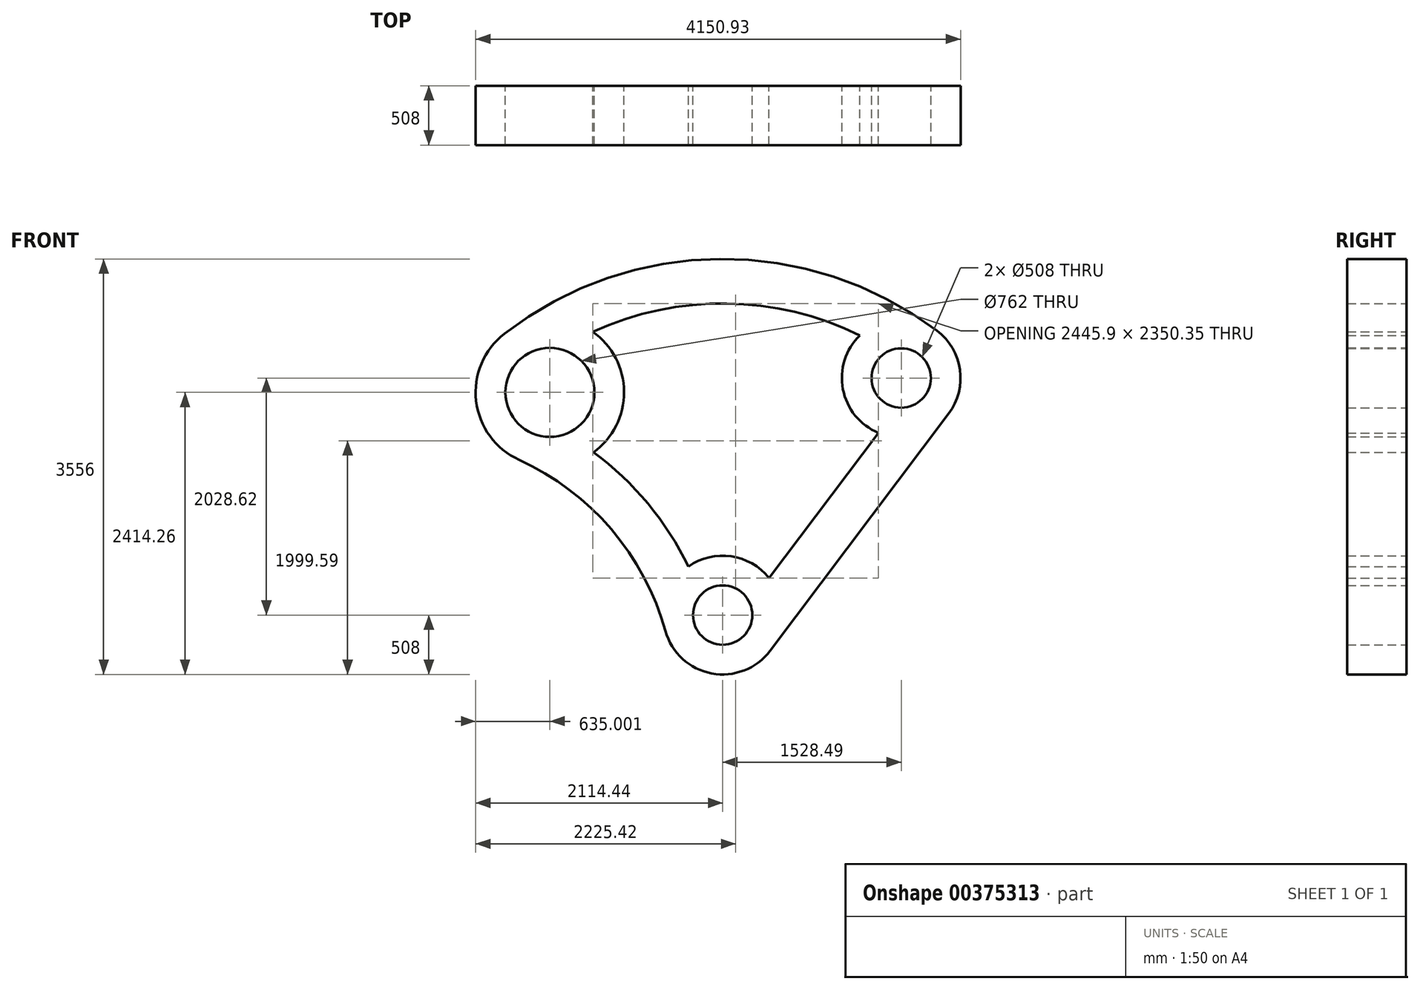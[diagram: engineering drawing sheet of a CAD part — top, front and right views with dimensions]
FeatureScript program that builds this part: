
annotation { "Feature Type Name" : "Feature", "Feature Type Description" : "" }
export const myFeature = defineFeature(function(context is Context, id is Id, definition is map)
    precondition{}
    {
        {
            var Q0;
            Q0=qCreatedBy(makeId("Front.planeOp"),FACE);
            var sketch = newSketch(context, id + "F0", { "sketchPlane" : qUnion([Q0])});
            skCircle(sketch, "E0", {"center": v(0, 0) * mm, "radius": 254 * mm});
            skArc(sketch, "E1", {"start": v(397.42, 316.42) * mm, "mid": v(71.94, 502.88) * mm, "end": v(-292.77, 415.15) * mm});
            skArc(sketch, "E2", {"start": v(-489.27, -136.66) * mm, "mid": v(-954.02, 734.53) * mm, "end": v(-1742.82, 1328.46) * mm});
            skCircle(sketch, "E3", {"center": v(1528.5, 2028.62) * mm, "radius": 254 * mm});
            skArc(sketch, "E4", {"start": v(1934.22, 1722.93) * mm, "mid": v(2031.54, 2099.35) * mm, "end": v(1834.19, 2434.35) * mm});
            skCircle(sketch, "E5", {"center": v(-1479.44, 1906.26) * mm, "radius": 381 * mm});
            skArc(sketch, "E6", {"start": v(-1868.76, 2407.9) * mm, "mid": v(-2110.16, 1832.67) * mm, "end": v(-1742.82, 1328.46) * mm});
            skArc(sketch, "E7", {"start": v(1834.19, 2434.35) * mm, "mid": v(-21.76, 3047.92) * mm, "end": v(-1868.76, 2407.9) * mm});
            skLineSegment(sketch, "E8", {"start": v(405.72, -305.7) * mm, "end": v(1934.22, 1722.93) * mm});
            skLineSegment(sketch, "E9", {"start": v(397.42, 316.42) * mm, "end": v(1333.93, 1559.36) * mm});
            skArc(sketch, "E10.trimOffspring", {"start": v(1175.51, 2393.96) * mm, "mid": v(35.17, 2666.77) * mm, "end": v(-1111.97, 2424.13) * mm});
            skArc(sketch, "E11.trimOffspring", {"start": v(1175.51, 2393.96) * mm, "mid": v(1029.4, 1933.9) * mm, "end": v(1333.93, 1559.36) * mm});
            skArc(sketch, "E12.trimOffspring", {"start": v(-1105.58, 1392.98) * mm, "mid": v(-844.45, 1910.2) * mm, "end": v(-1111.97, 2424.13) * mm});
            skArc(sketch, "E13.trimOffspring", {"start": v(-489.27, -136.66) * mm, "mid": v(-94.28, -499.17) * mm, "end": v(405.72, -305.7) * mm});
            skArc(sketch, "E14.trimOffspring", {"start": v(-292.77, 415.15) * mm, "mid": v(-640.05, 953.21) * mm, "end": v(-1105.58, 1392.98) * mm});
            skSolve(sketch);
        }
        {
            var Q0;
            Q0=makeQuery(id+"F0.imprint","IMPRINT",FACE,{"disambiguationData":[TD([[makeQuery(id+"F0.imprint","IMPRINT",EDGE,{"derivedFrom":sQuery(id+"F0.wireOp",EDGE,"E0")}),-1.0]])]});
            extrude(context, id + "F1", {"entities" : qUnion([Q0]), "depth" : 508 * mm});
        }
    });
